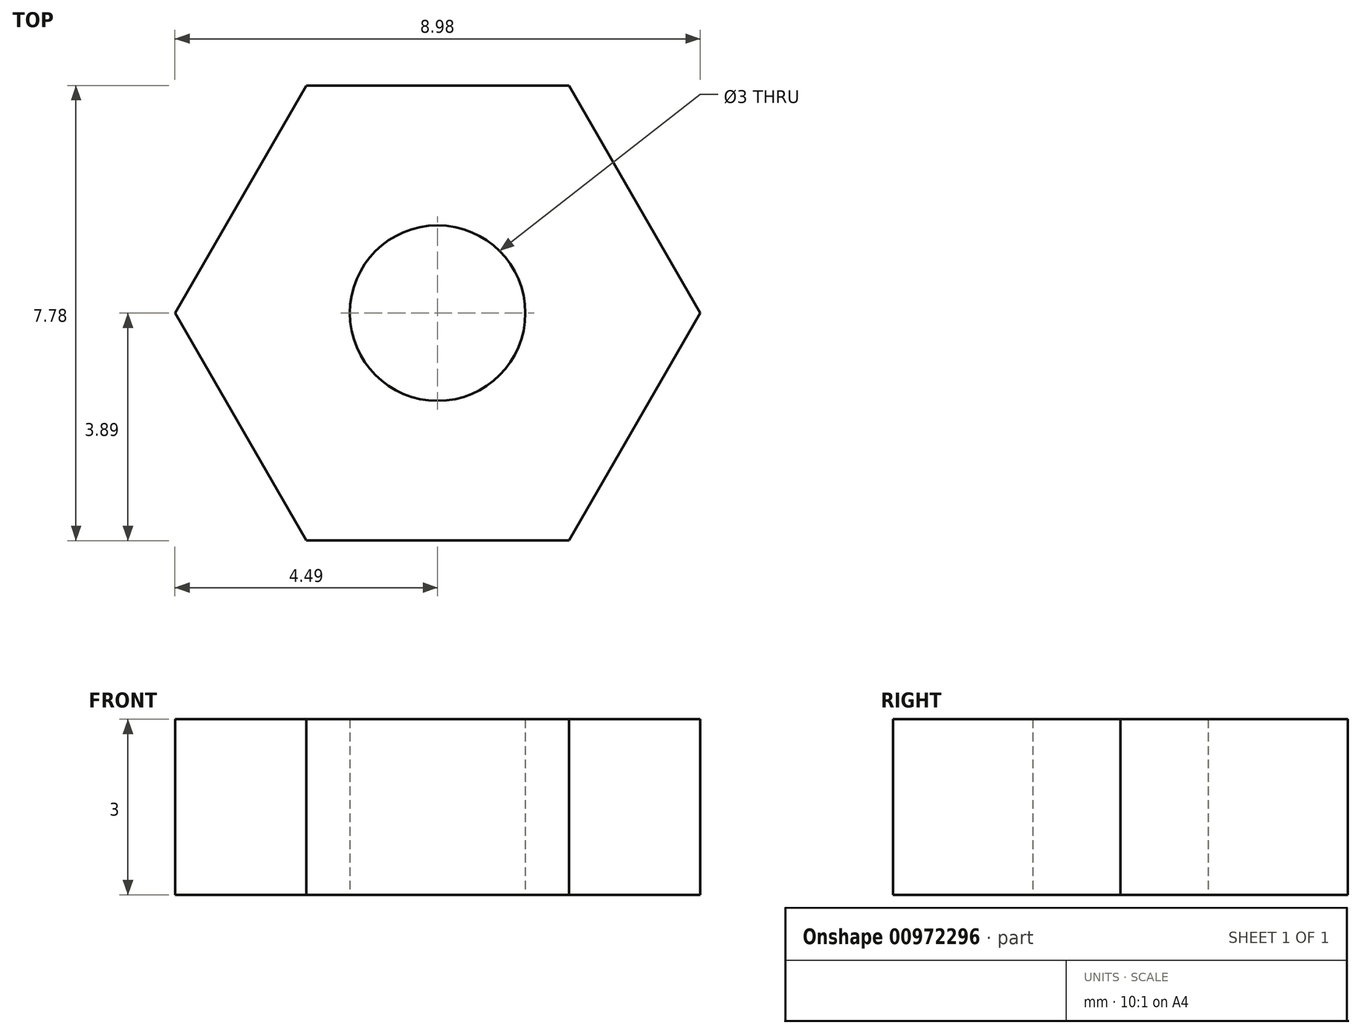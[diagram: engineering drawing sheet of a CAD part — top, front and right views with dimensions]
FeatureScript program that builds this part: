
annotation { "Feature Type Name" : "Feature", "Feature Type Description" : "" }
export const myFeature = defineFeature(function(context is Context, id is Id, definition is map)
    precondition{}
    {
        {
            var Q0;
            Q0=qCreatedBy(makeId("Top.planeOp"),FACE);
            var sketch = newSketch(context, id + "F0", { "sketchPlane" : qUnion([Q0])});
            skCircle(sketch, "E0.cCircle", {"center": v(0, 0) * mm, "radius": 3.89 * mm, "construction": true});
            skLineSegment(sketch, "E0.0", {"start": v(-2.24, 3.89) * mm, "end": v(2.24, 3.89) * mm});
            skLineSegment(sketch, "E0.1", {"start": v(2.24, 3.89) * mm, "end": v(4.49, 0) * mm});
            skLineSegment(sketch, "E0.2", {"start": v(4.49, 0) * mm, "end": v(2.24, -3.89) * mm});
            skLineSegment(sketch, "E0.3", {"start": v(2.24, -3.89) * mm, "end": v(-2.24, -3.89) * mm});
            skLineSegment(sketch, "E0.4", {"start": v(-2.24, -3.89) * mm, "end": v(-4.49, 0) * mm});
            skLineSegment(sketch, "E0.5", {"start": v(-4.49, 0) * mm, "end": v(-2.24, 3.89) * mm});
            skPoint(sketch, "E0.0.midPoint", {"position": v(0, 3.89) * mm});
            skCircle(sketch, "E1", {"center": v(0, 0) * mm, "radius": 1.5 * mm});
            skLineSegment(sketch, "E2", {"start": v(-4.49, 0) * mm, "end": v(4.49, 0) * mm, "construction": true});
            skSolve(sketch);
        }
        {
            var Q0;
            Q0=makeQuery(id+"F0.imprint","IMPRINT",FACE,{"disambiguationData":[TD([[makeQuery(id+"F0.imprint","IMPRINT",EDGE,{"derivedFrom":sQuery(id+"F0.wireOp",EDGE,"E0.0")}),-1.0]])]});
            extrude(context, id + "F1", {"entities" : qUnion([Q0]), "depth" : 3 * mm, "offsetDistance" : 25 * mm});
        }
    });
